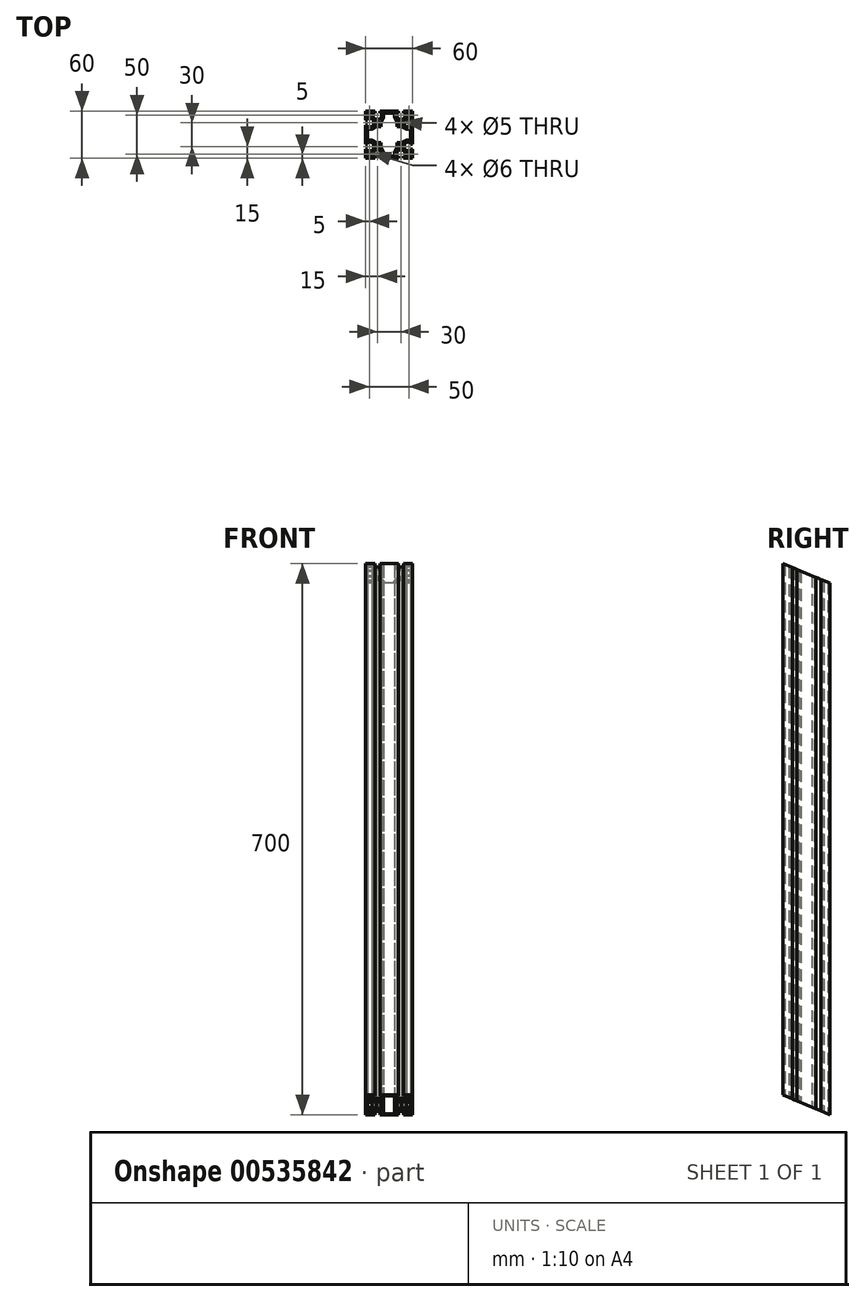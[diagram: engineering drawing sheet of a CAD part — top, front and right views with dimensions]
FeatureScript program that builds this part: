
annotation { "Feature Type Name" : "Feature", "Feature Type Description" : "" }
export const myFeature = defineFeature(function(context is Context, id is Id, definition is map)
    precondition{}
    {
        {
            var Q0;
            Q0=qCreatedBy(makeId("Top.planeOp"),FACE);
            var sketch = newSketch(context, id + "F0", { "sketchPlane" : qUnion([Q0])});
            skLineSegment(sketch, "E0.bottom", {"start": v(30, -30) * mm, "end": v(-30, -30) * mm});
            skLineSegment(sketch, "E0.top", {"start": v(30, 30) * mm, "end": v(-30, 30) * mm});
            skLineSegment(sketch, "E0.left", {"start": v(30, -30) * mm, "end": v(30, 30) * mm});
            skLineSegment(sketch, "E0.right", {"start": v(-30, -30) * mm, "end": v(-30, 30) * mm});
            skPoint(sketch, "E0.middle", {"position": v(0, 0) * mm});
            skLineSegment(sketch, "E1.top", {"start": v(-11.85, 30) * mm, "end": v(-18.15, 30) * mm});
            skLineSegment(sketch, "E1.left", {"start": v(-11.85, 27.5) * mm, "end": v(-11.85, 30) * mm});
            skLineSegment(sketch, "E1.right", {"start": v(-18.15, 27.5) * mm, "end": v(-18.15, 30) * mm});
            skPoint(sketch, "E1.middle", {"position": v(-15, 28.75) * mm});
            skLineSegment(sketch, "E2.bottom", {"start": v(-9.85, 27.5) * mm, "end": v(-11.85, 27.5) * mm});
            skLineSegment(sketch, "E2.left", {"start": v(-9.85, 27.5) * mm, "end": v(-9.85, 21.55) * mm});
            skLineSegment(sketch, "E2.right", {"start": v(-20.15, 27.5) * mm, "end": v(-20.15, 21.55) * mm});
            skPoint(sketch, "E2.middle", {"position": v(-15, 24.52) * mm});
            skArc(sketch, "E3", {"start": v(-20.15, 21.55) * mm, "mid": v(-15, 19.5) * mm, "end": v(-9.85, 21.55) * mm});
            skPoint(sketch, "E4.MirrorP", {"position": v(15, 24.52) * mm});
            skPoint(sketch, "E5.MirrorP", {"position": v(15, 28.75) * mm});
            skLineSegment(sketch, "E6.MirrorCS", {"start": v(11.85, 27.5) * mm, "end": v(11.85, 30) * mm});
            skLineSegment(sketch, "E7.MirrorCS", {"start": v(18.15, 27.5) * mm, "end": v(18.15, 30) * mm});
            skLineSegment(sketch, "E8.MirrorCS", {"start": v(9.85, 27.5) * mm, "end": v(11.85, 27.5) * mm});
            skLineSegment(sketch, "E9.MirrorCS", {"start": v(9.85, 27.5) * mm, "end": v(9.85, 21.55) * mm});
            skArc(sketch, "E10.MirrorCS", {"start": v(20.15, 21.55) * mm, "mid": v(15, 19.5) * mm, "end": v(9.85, 21.55) * mm});
            skLineSegment(sketch, "E11.MirrorCS", {"start": v(20.15, 27.5) * mm, "end": v(20.15, 21.55) * mm});
            skLineSegment(sketch, "E12.MirrorCS", {"start": v(11.85, 30) * mm, "end": v(18.15, 30) * mm});
            skLineSegment(sketch, "E13.1.0", {"start": v(27.5, 20.15) * mm, "end": v(21.55, 20.15) * mm});
            skLineSegment(sketch, "E13.1.1", {"start": v(27.5, 9.85) * mm, "end": v(21.55, 9.85) * mm});
            skArc(sketch, "E13.1.2", {"start": v(21.55, 20.15) * mm, "mid": v(19.5, 15) * mm, "end": v(21.55, 9.85) * mm});
            skLineSegment(sketch, "E13.1.3", {"start": v(27.5, -9.85) * mm, "end": v(21.55, -9.85) * mm});
            skLineSegment(sketch, "E13.1.4", {"start": v(27.5, -20.15) * mm, "end": v(21.55, -20.15) * mm});
            skPoint(sketch, "E13.1.5", {"position": v(28.75, 15) * mm});
            skPoint(sketch, "E13.1.6", {"position": v(28.75, -15) * mm});
            skArc(sketch, "E13.1.7", {"start": v(21.55, -20.15) * mm, "mid": v(19.5, -15) * mm, "end": v(21.55, -9.85) * mm});
            skPoint(sketch, "E13.1.8", {"position": v(24.52, -15) * mm});
            skPoint(sketch, "E13.1.9", {"position": v(24.52, 15) * mm});
            skLineSegment(sketch, "E13.1.10", {"start": v(27.5, 9.85) * mm, "end": v(27.5, 20.15) * mm});
            skLineSegment(sketch, "E13.1.11", {"start": v(27.5, -11.85) * mm, "end": v(27.5, -18.15) * mm});
            skLineSegment(sketch, "E13.1.12", {"start": v(30, 11.85) * mm, "end": v(30, 18.15) * mm});
            skLineSegment(sketch, "E13.1.13", {"start": v(30, -11.85) * mm, "end": v(30, -18.15) * mm});
            skLineSegment(sketch, "E13.1.14", {"start": v(27.5, 18.15) * mm, "end": v(30, 18.15) * mm});
            skLineSegment(sketch, "E13.1.15", {"start": v(27.5, 11.85) * mm, "end": v(30, 11.85) * mm});
            skLineSegment(sketch, "E13.1.16", {"start": v(27.5, 11.85) * mm, "end": v(27.5, 18.15) * mm});
            skLineSegment(sketch, "E13.1.17", {"start": v(27.5, -9.85) * mm, "end": v(27.5, -20.15) * mm});
            skLineSegment(sketch, "E13.1.18", {"start": v(27.5, -18.15) * mm, "end": v(30, -18.15) * mm});
            skLineSegment(sketch, "E13.1.19", {"start": v(27.5, -11.85) * mm, "end": v(30, -11.85) * mm});
            skLineSegment(sketch, "E13.2.0", {"start": v(20.15, -27.5) * mm, "end": v(20.15, -21.55) * mm});
            skLineSegment(sketch, "E13.2.1", {"start": v(9.85, -27.5) * mm, "end": v(9.85, -21.55) * mm});
            skArc(sketch, "E13.2.2", {"start": v(20.15, -21.55) * mm, "mid": v(15, -19.5) * mm, "end": v(9.85, -21.55) * mm});
            skLineSegment(sketch, "E13.2.3", {"start": v(-9.85, -27.5) * mm, "end": v(-9.85, -21.55) * mm});
            skLineSegment(sketch, "E13.2.4", {"start": v(-20.15, -27.5) * mm, "end": v(-20.15, -21.55) * mm});
            skPoint(sketch, "E13.2.5", {"position": v(15, -28.75) * mm});
            skPoint(sketch, "E13.2.6", {"position": v(-15, -28.75) * mm});
            skArc(sketch, "E13.2.7", {"start": v(-20.15, -21.55) * mm, "mid": v(-15, -19.5) * mm, "end": v(-9.85, -21.55) * mm});
            skPoint(sketch, "E13.2.8", {"position": v(-15, -24.52) * mm});
            skPoint(sketch, "E13.2.9", {"position": v(15, -24.52) * mm});
            skLineSegment(sketch, "E13.2.10", {"start": v(9.85, -27.5) * mm, "end": v(20.15, -27.5) * mm});
            skLineSegment(sketch, "E13.2.11", {"start": v(-11.85, -27.5) * mm, "end": v(-18.15, -27.5) * mm});
            skLineSegment(sketch, "E13.2.12", {"start": v(11.85, -30) * mm, "end": v(18.15, -30) * mm});
            skLineSegment(sketch, "E13.2.13", {"start": v(-11.85, -30) * mm, "end": v(-18.15, -30) * mm});
            skLineSegment(sketch, "E13.2.14", {"start": v(18.15, -27.5) * mm, "end": v(18.15, -30) * mm});
            skLineSegment(sketch, "E13.2.15", {"start": v(11.85, -27.5) * mm, "end": v(11.85, -30) * mm});
            skLineSegment(sketch, "E13.2.16", {"start": v(11.85, -27.5) * mm, "end": v(18.15, -27.5) * mm});
            skLineSegment(sketch, "E13.2.17", {"start": v(-9.85, -27.5) * mm, "end": v(-20.15, -27.5) * mm});
            skLineSegment(sketch, "E13.2.18", {"start": v(-18.15, -27.5) * mm, "end": v(-18.15, -30) * mm});
            skLineSegment(sketch, "E13.2.19", {"start": v(-11.85, -27.5) * mm, "end": v(-11.85, -30) * mm});
            skLineSegment(sketch, "E13.3.0", {"start": v(-27.5, -20.15) * mm, "end": v(-21.55, -20.15) * mm});
            skLineSegment(sketch, "E13.3.1", {"start": v(-27.5, -9.85) * mm, "end": v(-21.55, -9.85) * mm});
            skArc(sketch, "E13.3.2", {"start": v(-21.55, -20.15) * mm, "mid": v(-19.5, -15) * mm, "end": v(-21.55, -9.85) * mm});
            skLineSegment(sketch, "E13.3.3", {"start": v(-27.5, 9.85) * mm, "end": v(-21.55, 9.85) * mm});
            skLineSegment(sketch, "E13.3.4", {"start": v(-27.5, 20.15) * mm, "end": v(-21.55, 20.15) * mm});
            skPoint(sketch, "E13.3.5", {"position": v(-28.75, -15) * mm});
            skPoint(sketch, "E13.3.6", {"position": v(-28.75, 15) * mm});
            skArc(sketch, "E13.3.7", {"start": v(-21.55, 20.15) * mm, "mid": v(-19.5, 15) * mm, "end": v(-21.55, 9.85) * mm});
            skPoint(sketch, "E13.3.8", {"position": v(-24.52, 15) * mm});
            skPoint(sketch, "E13.3.9", {"position": v(-24.52, -15) * mm});
            skLineSegment(sketch, "E13.3.10", {"start": v(-27.5, -9.85) * mm, "end": v(-27.5, -20.15) * mm});
            skLineSegment(sketch, "E13.3.11", {"start": v(-27.5, 11.85) * mm, "end": v(-27.5, 18.15) * mm});
            skLineSegment(sketch, "E13.3.12", {"start": v(-30, -11.85) * mm, "end": v(-30, -18.15) * mm});
            skLineSegment(sketch, "E13.3.13", {"start": v(-30, 11.85) * mm, "end": v(-30, 18.15) * mm});
            skLineSegment(sketch, "E13.3.14", {"start": v(-27.5, -18.15) * mm, "end": v(-30, -18.15) * mm});
            skLineSegment(sketch, "E13.3.15", {"start": v(-27.5, -11.85) * mm, "end": v(-30, -11.85) * mm});
            skLineSegment(sketch, "E13.3.16", {"start": v(-27.5, -11.85) * mm, "end": v(-27.5, -18.15) * mm});
            skLineSegment(sketch, "E13.3.17", {"start": v(-27.5, 9.85) * mm, "end": v(-27.5, 20.15) * mm});
            skLineSegment(sketch, "E13.3.18", {"start": v(-27.5, 18.15) * mm, "end": v(-30, 18.15) * mm});
            skLineSegment(sketch, "E13.3.19", {"start": v(-27.5, 11.85) * mm, "end": v(-30, 11.85) * mm});
            skLineSegment(sketch, "E13.anchor1", {"start": v(0, 0) * mm, "end": v(-20.15, 21.55) * mm, "construction": true});
            skLineSegment(sketch, "E13.anchor2", {"start": v(0, 0) * mm, "end": v(-21.55, -20.15) * mm, "construction": true});
            skLineSegment(sketch, "E14.trimOffspring", {"start": v(-18.15, 27.5) * mm, "end": v(-20.15, 27.5) * mm});
            skLineSegment(sketch, "E15.trimOffspring", {"start": v(18.15, 27.5) * mm, "end": v(20.15, 27.5) * mm});
            skCircle(sketch, "E16", {"center": v(-15, 15) * mm, "radius": 2.5 * mm});
            skCircle(sketch, "E17", {"center": v(-25, 25) * mm, "radius": 3 * mm});
            skCircle(sketch, "E18.MirrorC", {"center": v(25, 25) * mm, "radius": 3 * mm});
            skCircle(sketch, "E19.MirrorC", {"center": v(25, -25) * mm, "radius": 3 * mm});
            skCircle(sketch, "E20.MirrorC", {"center": v(-25, -25) * mm, "radius": 3 * mm});
            skCircle(sketch, "E21.MirrorC", {"center": v(15, 15) * mm, "radius": 2.5 * mm});
            skCircle(sketch, "E22.MirrorC", {"center": v(15, -15) * mm, "radius": 2.5 * mm});
            skCircle(sketch, "E23.MirrorC", {"center": v(-15, -15) * mm, "radius": 2.5 * mm});
            skLineSegment(sketch, "E24", {"start": v(-7, 27.5) * mm, "end": v(0, 27.5) * mm});
            skLineSegment(sketch, "E25", {"start": v(-7, 27.5) * mm, "end": v(-7, 22) * mm});
            skLineSegment(sketch, "E26", {"start": v(-10, 10) * mm, "end": v(-10, 16) * mm});
            skLineSegment(sketch, "E27", {"start": v(-10, 16) * mm, "end": v(-7, 22) * mm});
            skLineSegment(sketch, "E28.MirrorCS", {"start": v(10, 10) * mm, "end": v(10, 16) * mm});
            skLineSegment(sketch, "E29.MirrorCS", {"start": v(10, 16) * mm, "end": v(7, 22) * mm});
            skLineSegment(sketch, "E30.MirrorCS", {"start": v(7, 27.5) * mm, "end": v(0, 27.5) * mm});
            skLineSegment(sketch, "E31.MirrorCS", {"start": v(7, 27.5) * mm, "end": v(7, 22) * mm});
            skLineSegment(sketch, "E32.1.0", {"start": v(-10, -10) * mm, "end": v(-16, -10) * mm});
            skLineSegment(sketch, "E32.1.1", {"start": v(-16, -10) * mm, "end": v(-22, -7) * mm});
            skLineSegment(sketch, "E32.1.2", {"start": v(-27.5, -7) * mm, "end": v(-22, -7) * mm});
            skLineSegment(sketch, "E32.1.3", {"start": v(-27.5, -7) * mm, "end": v(-27.5, 0) * mm});
            skLineSegment(sketch, "E32.1.4", {"start": v(-27.5, 7) * mm, "end": v(-27.5, 0) * mm});
            skLineSegment(sketch, "E32.1.5", {"start": v(-27.5, 7) * mm, "end": v(-22, 7) * mm});
            skLineSegment(sketch, "E32.1.6", {"start": v(-16, 10) * mm, "end": v(-22, 7) * mm});
            skLineSegment(sketch, "E32.1.7", {"start": v(-10, 10) * mm, "end": v(-16, 10) * mm});
            skLineSegment(sketch, "E32.2.0", {"start": v(10, -10) * mm, "end": v(10, -16) * mm});
            skLineSegment(sketch, "E32.2.1", {"start": v(10, -16) * mm, "end": v(7, -22) * mm});
            skLineSegment(sketch, "E32.2.2", {"start": v(7, -27.5) * mm, "end": v(7, -22) * mm});
            skLineSegment(sketch, "E32.2.3", {"start": v(7, -27.5) * mm, "end": v(0, -27.5) * mm});
            skLineSegment(sketch, "E32.2.4", {"start": v(-7, -27.5) * mm, "end": v(0, -27.5) * mm});
            skLineSegment(sketch, "E32.2.5", {"start": v(-7, -27.5) * mm, "end": v(-7, -22) * mm});
            skLineSegment(sketch, "E32.2.6", {"start": v(-10, -16) * mm, "end": v(-7, -22) * mm});
            skLineSegment(sketch, "E32.2.7", {"start": v(-10, -10) * mm, "end": v(-10, -16) * mm});
            skLineSegment(sketch, "E32.3.0", {"start": v(10, 10) * mm, "end": v(16, 10) * mm});
            skLineSegment(sketch, "E32.3.1", {"start": v(16, 10) * mm, "end": v(22, 7) * mm});
            skLineSegment(sketch, "E32.3.2", {"start": v(27.5, 7) * mm, "end": v(22, 7) * mm});
            skLineSegment(sketch, "E32.3.3", {"start": v(27.5, 7) * mm, "end": v(27.5, 0) * mm});
            skLineSegment(sketch, "E32.3.4", {"start": v(27.5, -7) * mm, "end": v(27.5, 0) * mm});
            skLineSegment(sketch, "E32.3.5", {"start": v(27.5, -7) * mm, "end": v(22, -7) * mm});
            skLineSegment(sketch, "E32.3.6", {"start": v(16, -10) * mm, "end": v(22, -7) * mm});
            skLineSegment(sketch, "E32.3.7", {"start": v(10, -10) * mm, "end": v(16, -10) * mm});
            skSolve(sketch);
        }
        {
            var Q0;
            {var subQ30=sQuery(id+"F0.wireOp",EDGE,"E1.left");Q0=makeQuery(id+"F0.imprint","IMPRINT",FACE,{"disambiguationData":[TD([[makeQuery(id+"F0.imprint","IMPRINT",EDGE,{"derivedFrom":subQ30}),-1.0]])]});}
            extrude(context, id + "F1", {"entities" : qUnion([Q0]), "depth" : 700 * mm, "offsetDistance" : 25 * mm});
        }
        {
            var Q0;
            Q0=makeQuery(id+"F1.opExtrude","SWEPT_EDGE",EDGE,{"disambiguationData":[OSD([sQuery(id+"F0.wireOp",EDGE,"E24"),sQuery(id+"F0.wireOp",EDGE,"E25")])]});
            var Q1;
            Q1=makeQuery(id+"F1.opExtrude","SWEPT_EDGE",EDGE,{"disambiguationData":[OSD([sQuery(id+"F0.wireOp",EDGE,"E30.MirrorCS"),sQuery(id+"F0.wireOp",EDGE,"E31.MirrorCS")])]});
            var Q2;
            Q2=makeQuery(id+"F1.opExtrude","SWEPT_EDGE",EDGE,{"disambiguationData":[OSD([sQuery(id+"F0.wireOp",EDGE,"840db5bc-c403-45cd-90c7-254e62d9e8c5.3.2"),sQuery(id+"F0.wireOp",EDGE,"840db5bc-c403-45cd-90c7-254e62d9e8c5.3.3")])]});
            var Q3;
            Q3=makeQuery(id+"F1.opExtrude","SWEPT_EDGE",EDGE,{"disambiguationData":[OSD([sQuery(id+"F0.wireOp",EDGE,"840db5bc-c403-45cd-90c7-254e62d9e8c5.3.4"),sQuery(id+"F0.wireOp",EDGE,"840db5bc-c403-45cd-90c7-254e62d9e8c5.3.5")])]});
            var Q4;
            Q4=makeQuery(id+"F1.opExtrude","SWEPT_EDGE",EDGE,{"disambiguationData":[OSD([sQuery(id+"F0.wireOp",EDGE,"840db5bc-c403-45cd-90c7-254e62d9e8c5.1.4"),sQuery(id+"F0.wireOp",EDGE,"840db5bc-c403-45cd-90c7-254e62d9e8c5.1.5")])]});
            var Q5;
            Q5=makeQuery(id+"F1.opExtrude","SWEPT_EDGE",EDGE,{"disambiguationData":[OSD([sQuery(id+"F0.wireOp",EDGE,"840db5bc-c403-45cd-90c7-254e62d9e8c5.1.2"),sQuery(id+"F0.wireOp",EDGE,"840db5bc-c403-45cd-90c7-254e62d9e8c5.1.3")])]});
            var Q6;
            Q6=makeQuery(id+"F1.opExtrude","SWEPT_EDGE",EDGE,{"disambiguationData":[OSD([sQuery(id+"F0.wireOp",EDGE,"840db5bc-c403-45cd-90c7-254e62d9e8c5.2.2"),sQuery(id+"F0.wireOp",EDGE,"840db5bc-c403-45cd-90c7-254e62d9e8c5.2.3")])]});
            var Q7;
            Q7=makeQuery(id+"F1.opExtrude","SWEPT_EDGE",EDGE,{"disambiguationData":[OSD([sQuery(id+"F0.wireOp",EDGE,"840db5bc-c403-45cd-90c7-254e62d9e8c5.2.4"),sQuery(id+"F0.wireOp",EDGE,"840db5bc-c403-45cd-90c7-254e62d9e8c5.2.5")])]});
            fillet(context, id + "F2", {"entities" : qUnion([Q0, Q1, Q2, Q3, Q4, Q5, Q6, Q7]), "radius" : 2 * mm, "tangentPropagation" : true, "allowEdgeOverflow" : false});
        }
        {
            var Q0;
            Q0=makeQuery(id+"F1.opExtrude","SWEPT_EDGE",EDGE,{"disambiguationData":[OSD([sQuery(id+"F0.wireOp",EDGE,"E26"),sQuery(id+"F0.wireOp",EDGE,"E27")])]});
            var Q1;
            Q1=makeQuery(id+"F1.opExtrude","SWEPT_EDGE",EDGE,{"disambiguationData":[OSD([sQuery(id+"F0.wireOp",EDGE,"E28.MirrorCS"),sQuery(id+"F0.wireOp",EDGE,"E29.MirrorCS")])]});
            var Q2;
            Q2=makeQuery(id+"F1.opExtrude","SWEPT_EDGE",EDGE,{"disambiguationData":[OSD([sQuery(id+"F0.wireOp",EDGE,"840db5bc-c403-45cd-90c7-254e62d9e8c5.3.0"),sQuery(id+"F0.wireOp",EDGE,"840db5bc-c403-45cd-90c7-254e62d9e8c5.3.1")])]});
            var Q3;
            Q3=makeQuery(id+"F1.opExtrude","SWEPT_EDGE",EDGE,{"disambiguationData":[OSD([sQuery(id+"F0.wireOp",EDGE,"840db5bc-c403-45cd-90c7-254e62d9e8c5.1.6"),sQuery(id+"F0.wireOp",EDGE,"840db5bc-c403-45cd-90c7-254e62d9e8c5.1.7")])]});
            var Q4;
            Q4=makeQuery(id+"F1.opExtrude","SWEPT_EDGE",EDGE,{"disambiguationData":[OSD([sQuery(id+"F0.wireOp",EDGE,"840db5bc-c403-45cd-90c7-254e62d9e8c5.1.0"),sQuery(id+"F0.wireOp",EDGE,"840db5bc-c403-45cd-90c7-254e62d9e8c5.1.1")])]});
            var Q5;
            Q5=makeQuery(id+"F1.opExtrude","SWEPT_EDGE",EDGE,{"disambiguationData":[OSD([sQuery(id+"F0.wireOp",EDGE,"840db5bc-c403-45cd-90c7-254e62d9e8c5.3.6"),sQuery(id+"F0.wireOp",EDGE,"840db5bc-c403-45cd-90c7-254e62d9e8c5.3.7")])]});
            var Q6;
            Q6=makeQuery(id+"F1.opExtrude","SWEPT_EDGE",EDGE,{"disambiguationData":[OSD([sQuery(id+"F0.wireOp",EDGE,"840db5bc-c403-45cd-90c7-254e62d9e8c5.2.0"),sQuery(id+"F0.wireOp",EDGE,"840db5bc-c403-45cd-90c7-254e62d9e8c5.2.1")])]});
            var Q7;
            Q7=makeQuery(id+"F1.opExtrude","SWEPT_EDGE",EDGE,{"disambiguationData":[OSD([sQuery(id+"F0.wireOp",EDGE,"840db5bc-c403-45cd-90c7-254e62d9e8c5.2.6"),sQuery(id+"F0.wireOp",EDGE,"840db5bc-c403-45cd-90c7-254e62d9e8c5.2.7")])]});
            fillet(context, id + "F3", {"entities" : qUnion([Q0, Q1, Q2, Q3, Q4, Q5, Q6, Q7]), "radius" : 7 * mm, "tangentPropagation" : true, "allowEdgeOverflow" : false});
        }
        {
            var Q0;
            {var subQ0=sQuery(id+"F0.wireOp",EDGE,"E0.bottom");Q0=makeQuery(id+"F1.opExtrude","SWEPT_FACE",FACE,{"disambiguationData":[OSD([subQ0]),TDD([makeQuery(id+"F0.imprint","IMPRINT",EDGE,{"disambiguationData":[TD([[makeQuery(id+"F0.imprint","INTERSECT",VERTEX,{"derivedFrom":[subQ0,sQuery(id+"F0.wireOp",EDGE,"E13.2.12"),sQuery(id+"F0.wireOp",EDGE,"E13.2.15")]}),-1.0]])],"derivedFrom":subQ0})])]});}
            var sketch = newSketch(context, id + "F4", { "sketchPlane" : qUnion([Q0])});
            skLineSegment(sketch, "E33.0", {"start": v(-18.15, 700) * mm, "end": v(-30, 700) * mm});
            skLineSegment(sketch, "E33.1", {"start": v(30, 700) * mm, "end": v(30, 0) * mm});
            skLineSegment(sketch, "E34", {"start": v(-30, 700) * mm, "end": v(30, 700) * mm});
            skLineSegment(sketch, "E35", {"start": v(30, 640) * mm, "end": v(-30, 700) * mm});
            skLineSegment(sketch, "E36.0", {"start": v(-18.15, 0) * mm, "end": v(-30, 0) * mm});
            skLineSegment(sketch, "E37", {"start": v(-30, 0) * mm, "end": v(30, 0) * mm});
            skLineSegment(sketch, "E38", {"start": v(30, 60) * mm, "end": v(-30, 0) * mm});
            skSolve(sketch);
        }
        {
            var Q0;
            Q0=qCreatedBy(makeId("Right.planeOp"),FACE);
            var sketch = newSketch(context, id + "F5", { "sketchPlane" : qUnion([Q0])});
            skLineSegment(sketch, "E39.bottom", {"start": v(-73.16, 42.73) * mm, "end": v(30, 0) * mm});
            skLineSegment(sketch, "E39.top", {"start": v(-138.82, -115.8) * mm, "end": v(-35.66, -158.52) * mm});
            skLineSegment(sketch, "E39.left", {"start": v(-73.16, 42.73) * mm, "end": v(-138.82, -115.8) * mm});
            skLineSegment(sketch, "E39.right", {"start": v(30, 0) * mm, "end": v(-35.66, -158.52) * mm});
            skLineSegment(sketch, "E40.bottom", {"start": v(61.73, 921.46) * mm, "end": v(194.23, 866.57) * mm});
            skLineSegment(sketch, "E40.top", {"start": v(-30, 700) * mm, "end": v(102.5, 645.12) * mm});
            skLineSegment(sketch, "E40.left", {"start": v(61.73, 921.46) * mm, "end": v(-30, 700) * mm});
            skLineSegment(sketch, "E40.right", {"start": v(194.23, 866.57) * mm, "end": v(102.5, 645.12) * mm});
            skSolve(sketch);
        }
        {
            var Q0;
            Q0 = qSketchRegion(id + "F5", true);
            extrude(context, id + "F6", {"entities" : qUnion([Q0]), "operationType" : NewBodyOperationType.REMOVE, "depth" : 30 * mm, "offsetDistance" : 25 * mm, "hasSecondDirection" : true, "secondDirectionOppositeDirection" : true, "secondDirectionDepth" : 30 * mm});
        }
    });
